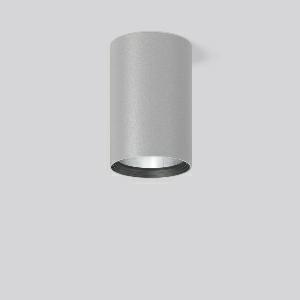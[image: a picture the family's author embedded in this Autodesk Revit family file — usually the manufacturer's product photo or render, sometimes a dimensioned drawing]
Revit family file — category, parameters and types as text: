
# Revit family: heledon_maxi_a_931240_004_76_120b
name_source: partatom
category: Lighting Fixtures
units: mm (PartAtom-declared; Revit-internal decimal feet)

## family parameters
Cut with Voids When Loaded = No
Host = Face
Light Source = No
Part Type = Normal
Room Calculation Point = No
Round Connector Dimension = Use Diameter
Shared = No

## types (1)
- HELEDON maxi A (1 x LED Modul 920 meat+, 2150 lm, 2000)
    Apparent Load = 33 VA
    Approval mark = CE
    CIE Flux Codes = 96 100 100 100 100
    Color Rendering = 90
    Color Temperature = 2000
    Default Elevation = 1800 mm
    Description = Series: HELEDON maxi
Cylindrical surface-mounted downlight. Housing: die-cast aluminium, powder-coated. Internal ceiling frame polycarbonate with bayonet mounting. Black plastic ring and recessed LED to prevent glare from the side. Optical assembly with reflector made of MIRO-Silver with 98% total light reflection for outstanding efficiency - can be changed without tools. Special LED for illumination of meat included. Suitable for Ceiling mounting. Easy installation with a separate ceiling frame with bayonet mounting and plug connection. Driver integrated. Connected via plug-in connector. High quality converter without flickering and stroboscopic effect. The following accessories can be mounted without use of tools: interchangeable lenses, decorative glasses, honeycomb louvre, clear and frosted diffusers, white interchangeable plastic ring. 
Colour: silver
Diameter: 123 mm
Height: 183 mm
Lamp: LED
Socket: without socket
Colour temperature: meat +
System power: 33 W
Rated luminous flux: 2150 lm
Luminous efficiency: 65 lm/W
Control gear: Converter, dimmable, DALI
Protection class: I
Type of protection: IP 20
    Height = 183 mm
    Lamp = 1 x LED Modul 920 meat+
    Lamp Light Flux = 2150 lm
    Lamp count = 1
    Length = 123 mm
    Lifetime = 50000 h
    Luminous efficacy = 65 lm/W
    Manufacturer = RZB
    ModVariant = No
    Model = 931240.004.76
    Mounting Place = Ceiling
    Mounting Type = Surface mounted
    Number of Poles = 1
    OnlyDefault = Yes
    Power Factor = 1
    Product Name = HELEDON maxi A
    Product group = Surface mounted downlights
    ProductGroupID = 302
    Protection Class = Protection class I
    Protection Degree = IP 20
    RLX_Detail_Level = 1
    RLX_Emergency_Light_Flux = 0 lm
    RLX_Emergency_Type = 0
    RLX_Emergency_Type_DB = No
    RlxData = <blob elided: 99233 chars, md5=fccc6c33>
    Socket = socket
    Standby Power = 0 W
    System Light Flux = 2150 lm
    System Power = 33 W
    Type Comments = Product without accessories
    Type Image = 931192.004.jpg
    URL = http://relux.com
    VarID = ---
    Voltage = 230 V
    Voltage Range = 220-240 V
    Weight = 0.00 kg
    Width = 0 mm  [stored 0 ft]

note: [stored X ft] marks values corroborated as IEEE doubles in the binary element streams (Revit-internal decimal feet)

## geometry (parser evidence)
native form markers: Blend x4, Sweep x11
no freeform markers — native parametric forms only
